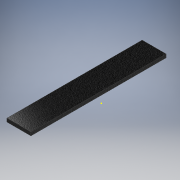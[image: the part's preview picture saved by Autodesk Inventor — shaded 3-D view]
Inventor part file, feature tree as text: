
AUTODESK INVENTOR PART (.ipt)
format: ipt  version: 2018 (Build 220112000, 112)  size: 98,816 bytes
history: native  units: in
note: dims shown in document units (in); Inventor stores cm internally (conversion verified against a paired STEP export)
features: sketch x2, extrude x1
ambient origin geometry x8: Origin, YZ Plane, XZ Plane, XY Plane, X Axis, Y Axis, Z Axis, Center Point
bodies: Solid1 (feature_tree)
feature tree (3):
  sketch  "Sketch1"  dims[d0=6.2205in d1=1.1024in]
  extrude  "Extrusion1"  Depth=1.1024in
  sketch  "Sketch2"  dims[d2=0.1575in d3=0.0in]
